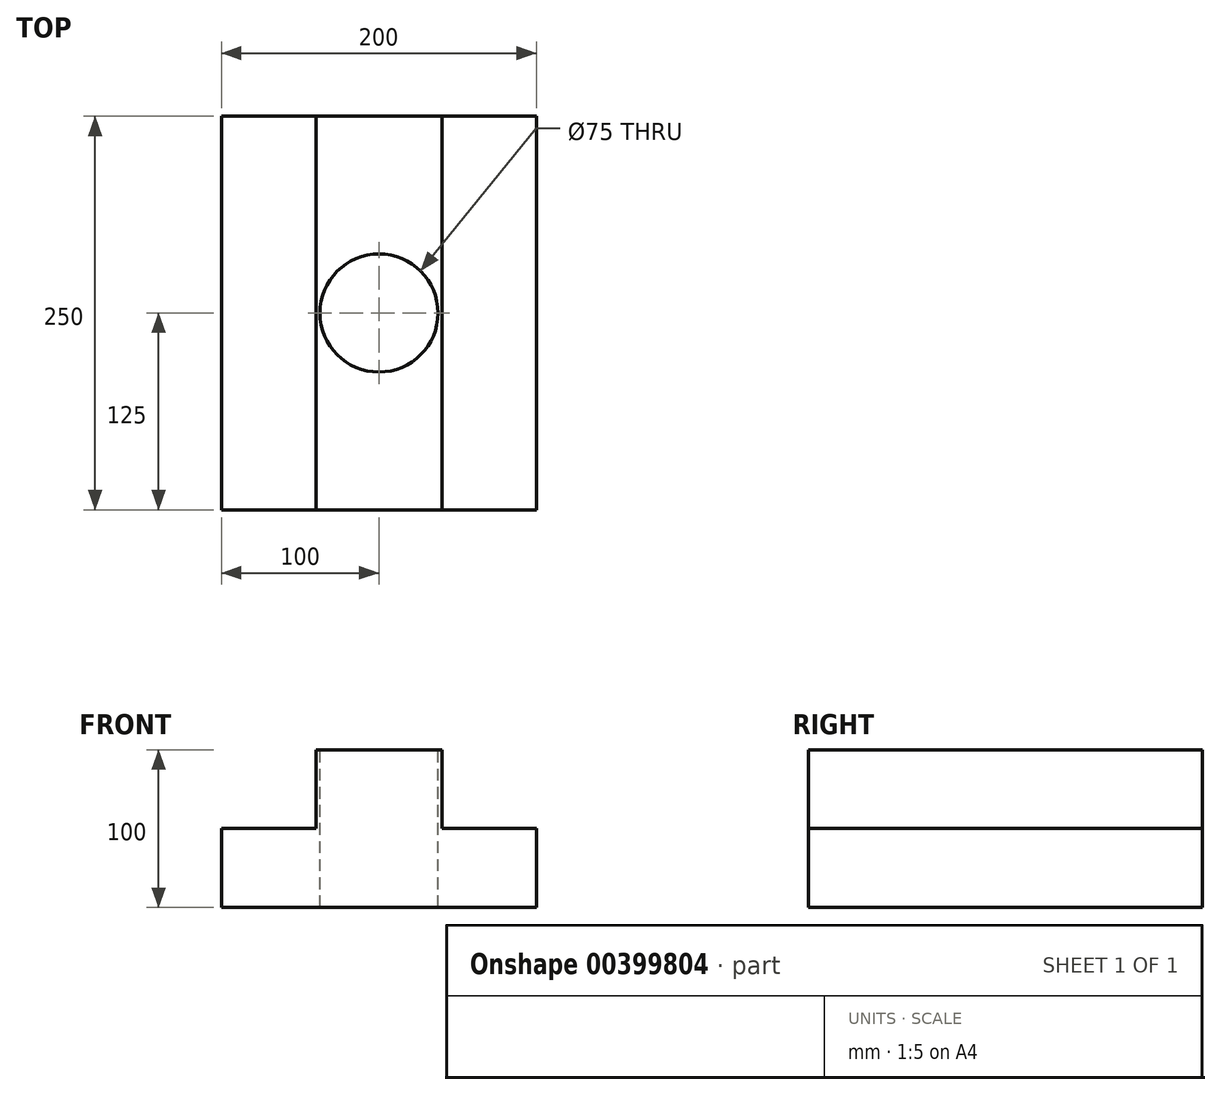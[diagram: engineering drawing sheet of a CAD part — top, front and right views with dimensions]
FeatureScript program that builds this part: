
annotation { "Feature Type Name" : "Feature", "Feature Type Description" : "" }
export const myFeature = defineFeature(function(context is Context, id is Id, definition is map)
    precondition{}
    {
        {
            var Q0;
            Q0=qCreatedBy(makeId("Top.planeOp"),FACE);
            var sketch = newSketch(context, id + "F0", { "sketchPlane" : qUnion([Q0])});
            skLineSegment(sketch, "E0.bottom", {"start": v(100, -125) * mm, "end": v(-100, -125) * mm});
            skLineSegment(sketch, "E0.top", {"start": v(100, 125) * mm, "end": v(-100, 125) * mm});
            skLineSegment(sketch, "E0.left", {"start": v(100, -125) * mm, "end": v(100, 125) * mm});
            skLineSegment(sketch, "E0.right", {"start": v(-100, -125) * mm, "end": v(-100, 125) * mm});
            skPoint(sketch, "E0.middle", {"position": v(0, 0) * mm});
            skSolve(sketch);
        }
        {
            var Q0;
            Q0=makeQuery(id+"F0.imprint","IMPRINT",FACE,{"disambiguationData":[TD([[makeQuery(id+"F0.imprint","IMPRINT",EDGE,{"derivedFrom":sQuery(id+"F0.wireOp",EDGE,"E0.bottom")}),-1.0]])]});
            extrude(context, id + "F1", {"entities" : qUnion([Q0]), "endBound" : BoundingType.SYMMETRIC, "depth" : 50 * mm});
        }
        {
            var Q0;
            Q0=makeQuery(id+"F1.opExtrude","CAP_FACE",FACE,{"disambiguationData":[OSD([sQuery(id+"F0.wireOp",EDGE,"E0.bottom"),sQuery(id+"F0.wireOp",EDGE,"E0.top"),sQuery(id+"F0.wireOp",EDGE,"E0.left"),sQuery(id+"F0.wireOp",EDGE,"E0.right")])],"isStart":false});
            var sketch = newSketch(context, id + "F2", { "sketchPlane" : qUnion([Q0])});
            skLineSegment(sketch, "E1.bottom", {"start": v(40, -125) * mm, "end": v(-40, -125) * mm});
            skLineSegment(sketch, "E1.top", {"start": v(40, 125) * mm, "end": v(-40, 125) * mm});
            skLineSegment(sketch, "E1.left", {"start": v(40, -125) * mm, "end": v(40, 125) * mm});
            skLineSegment(sketch, "E1.right", {"start": v(-40, -125) * mm, "end": v(-40, 125) * mm});
            skPoint(sketch, "E1.middle", {"position": v(0, 0) * mm});
            skSolve(sketch);
        }
        {
            var Q0;
            Q0=makeQuery(id+"F2.imprint","IMPRINT",FACE,{"disambiguationData":[TD([[makeQuery(id+"F2.imprint","IMPRINT",EDGE,{"derivedFrom":sQuery(id+"F2.wireOp",EDGE,"E1.bottom")}),-1.0]])]});
            extrude(context, id + "F3", {"entities" : qUnion([Q0]), "operationType" : NewBodyOperationType.ADD, "depth" : 50 * mm});
        }
        {
            var Q0;
            Q0=makeQuery(id+"F3.opExtrude","CAP_FACE",FACE,{"disambiguationData":[OSD([sQuery(id+"F2.wireOp",EDGE,"E1.bottom"),sQuery(id+"F2.wireOp",EDGE,"E1.top"),sQuery(id+"F2.wireOp",EDGE,"E1.left"),sQuery(id+"F2.wireOp",EDGE,"E1.right")])],"isStart":false});
            var sketch = newSketch(context, id + "F4", { "sketchPlane" : qUnion([Q0])});
            skCircle(sketch, "E2", {"center": v(0, 0) * mm, "radius": 37.5 * mm});
            skSolve(sketch);
        }
        {
            var Q0;
            Q0=makeQuery(id+"F4.imprint","IMPRINT",FACE,{"disambiguationData":[TD([[makeQuery(id+"F4.imprint","IMPRINT",EDGE,{"derivedFrom":sQuery(id+"F4.wireOp",EDGE,"E2")}),1.0]])]});
            extrude(context, id + "F5", {"entities" : qUnion([Q0]), "operationType" : NewBodyOperationType.REMOVE, "oppositeDirection" : true, "depth" : 137 * mm});
        }
    });
